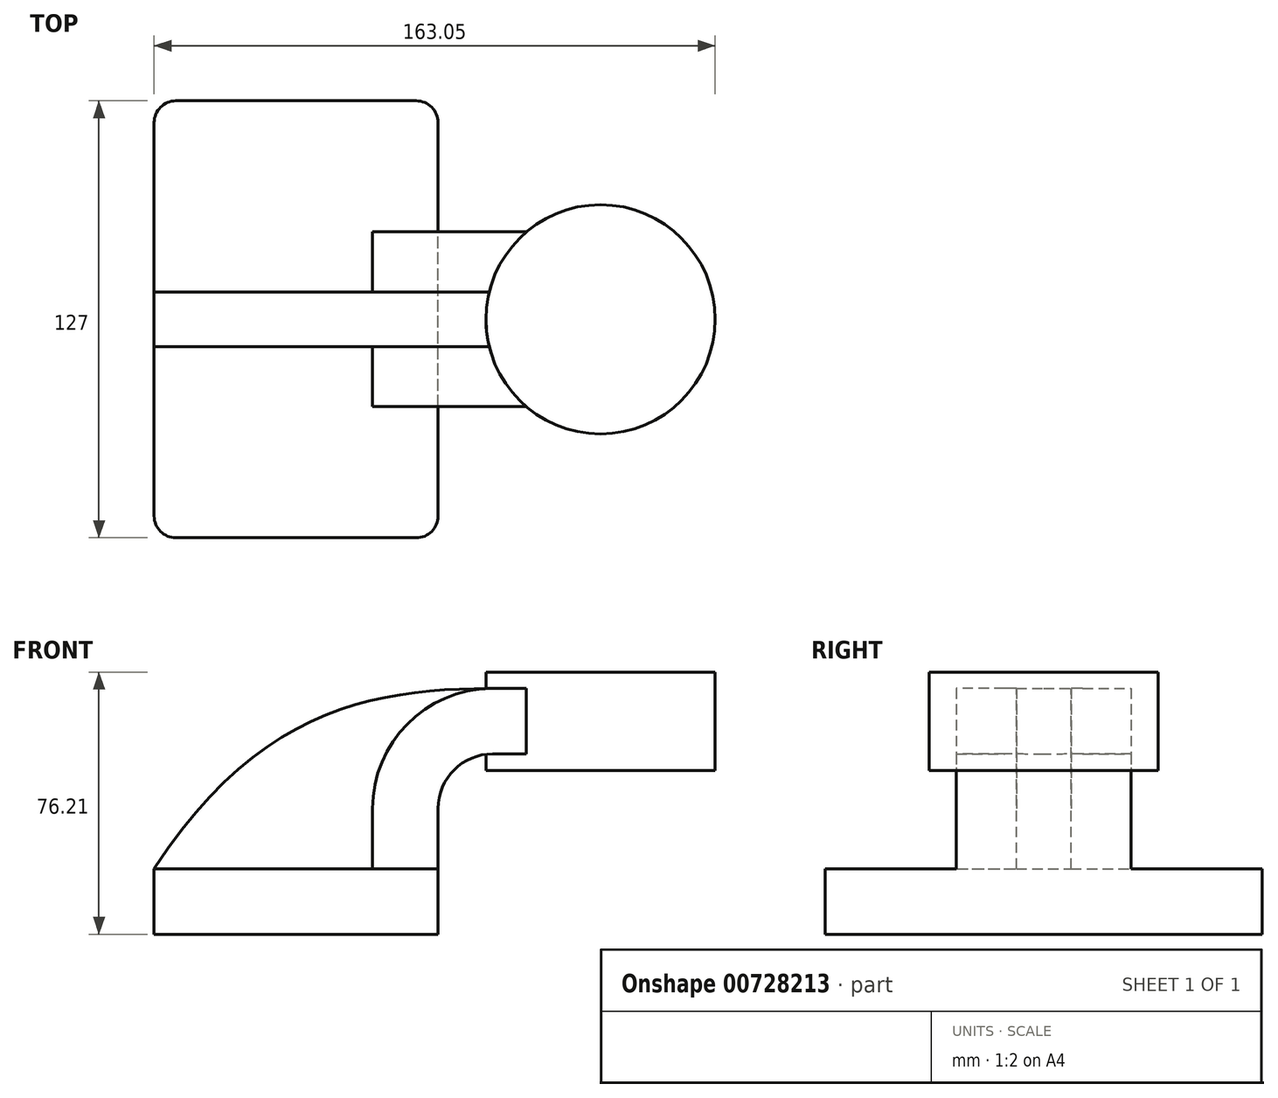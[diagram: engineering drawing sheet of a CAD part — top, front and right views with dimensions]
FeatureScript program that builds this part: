
annotation { "Feature Type Name" : "Feature", "Feature Type Description" : "" }
export const myFeature = defineFeature(function(context is Context, id is Id, definition is map)
    precondition{}
    {
        {
            var Q0;
            Q0=qCreatedBy(makeId("Front.planeOp"),FACE);
            var sketch = newSketch(context, id + "F0", { "sketchPlane" : qUnion([Q0])});
            skLineSegment(sketch, "E0.bottom", {"start": v(41.27, 9.53) * mm, "end": v(-41.28, 9.53) * mm});
            skLineSegment(sketch, "E0.top", {"start": v(41.28, -9.52) * mm, "end": v(-41.27, -9.52) * mm});
            skLineSegment(sketch, "E0.left", {"start": v(41.28, 9.53) * mm, "end": v(41.28, -9.52) * mm});
            skLineSegment(sketch, "E0.right", {"start": v(-41.28, 9.53) * mm, "end": v(-41.27, -9.52) * mm});
            skPoint(sketch, "E0.middle", {"position": v(0, 0) * mm});
            skLineSegment(sketch, "E1.bottom", {"start": v(70.97, 66.68) * mm, "end": v(121.77, 66.68) * mm});
            skLineSegment(sketch, "E1.top", {"start": v(70.97, 38.1) * mm, "end": v(121.77, 38.1) * mm});
            skLineSegment(sketch, "E1.left", {"start": v(70.97, 66.68) * mm, "end": v(70.97, 38.1) * mm});
            skLineSegment(sketch, "E1.right", {"start": v(121.77, 66.68) * mm, "end": v(121.77, 38.1) * mm});
            skPoint(sketch, "E1.middle", {"position": v(96.37, 52.39) * mm});
            skLineSegment(sketch, "E2", {"start": v(41.27, 9.53) * mm, "end": v(41.27, 27) * mm});
            skArc(sketch, "E3", {"start": v(41.27, 27) * mm, "mid": v(45.92, 38.23) * mm, "end": v(57.15, 42.88) * mm});
            skLineSegment(sketch, "E4", {"start": v(57.15, 42.88) * mm, "end": v(88.47, 42.88) * mm});
            skLineSegment(sketch, "E5.0", {"start": v(57.15, 61.93) * mm, "end": v(88.47, 61.93) * mm});
            skArc(sketch, "E5.1", {"start": v(22.23, 27) * mm, "mid": v(32.45, 51.7) * mm, "end": v(57.15, 61.93) * mm});
            skLineSegment(sketch, "E5.2", {"start": v(22.22, 9.53) * mm, "end": v(22.22, 27) * mm});
            skLineSegment(sketch, "E6", {"start": v(88.47, 42.88) * mm, "end": v(88.47, 61.93) * mm});
            skLineSegment(sketch, "E7", {"start": v(88.47, 61.93) * mm, "end": v(88.47, 66.68) * mm});
            skLineSegment(sketch, "E8", {"start": v(88.47, 42.88) * mm, "end": v(88.47, 38.1) * mm});
            skFitSpline(sketch, "E9", {"points": [v(-41.28, 9.52) * mm, v(57.15, 61.93) * mm], "startDerivative": vector(92.37, 142.7) * mm, "endDerivative": vector(100.21, 0.57) * mm});
            skSolve(sketch);
        }
        {
            var Q0;
            Q0=makeQuery(id+"F0.imprint","IMPRINT",FACE,{"disambiguationData":[TD([[makeQuery(id+"F0.imprint","IMPRINT",EDGE,{"derivedFrom":sQuery(id+"F0.wireOp",EDGE,"E0.top")}),-1.0]])]});
            extrude(context, id + "F1", {"entities" : qUnion([Q0]), "endBound" : BoundingType.SYMMETRIC, "depth" : 127 * mm, "offsetDistance" : 25.4 * mm});
        }
        {
            var Q0;
            {var subQ1=sQuery(id+"F0.wireOp",EDGE,"E2");Q0=makeQuery(id+"F0.imprint","IMPRINT",FACE,{"disambiguationData":[TD([[makeQuery(id+"F0.imprint","IMPRINT",EDGE,{"derivedFrom":subQ1}),1.0]])]});}
            var Q1;
            {var subQ5=sQuery(id+"F0.wireOp",EDGE,"E6");Q1=makeQuery(id+"F0.imprint","IMPRINT",FACE,{"disambiguationData":[TD([[makeQuery(id+"F0.imprint","IMPRINT",EDGE,{"derivedFrom":subQ5}),1.0]])]});}
            extrude(context, id + "F2", {"entities" : qUnion([Q0, Q1]), "operationType" : NewBodyOperationType.ADD, "endBound" : BoundingType.SYMMETRIC, "depth" : 50.8 * mm, "offsetDistance" : 25.4 * mm});
        }
        {
            var Q0;
            {var subQ3=sQuery(id+"F0.wireOp",EDGE,"E5.2");Q0=makeQuery(id+"F0.imprint","IMPRINT",FACE,{"disambiguationData":[TD([[makeQuery(id+"F0.imprint","IMPRINT",EDGE,{"derivedFrom":subQ3}),1.0]])]});}
            extrude(context, id + "F3", {"entities" : qUnion([Q0]), "operationType" : NewBodyOperationType.ADD, "endBound" : BoundingType.SYMMETRIC, "depth" : 15.88 * mm, "offsetDistance" : 25.4 * mm});
        }
        {
            var Q0;
            {var subQ0=sQuery(id+"F0.wireOp",EDGE,"E1.right");Q0=makeQuery(id+"F0.imprint","IMPRINT",FACE,{"disambiguationData":[TD([[makeQuery(id+"F0.imprint","IMPRINT",EDGE,{"derivedFrom":subQ0}),-1.0]])]});}
            var Q1;
            Q1=sQuery(id+"F0.wireOp",EDGE,"E6");
            revolve(context, id + "F4", {"operationType" : NewBodyOperationType.ADD, "surfaceOperationType" : NewSurfaceOperationType.NEW, "entities" : qUnion([Q0]), "axis" : qUnion([Q1]), "revolveType" : RevolveType.FULL});
        }
        {
            var Q0;
            Q0=makeQuery(id+"F1.opExtrude","CAP_EDGE",EDGE,{"disambiguationData":[OSD([sQuery(id+"F0.wireOp",EDGE,"E0.left")])],"isStart":false});
            var Q1;
            Q1=makeQuery(id+"F1.opExtrude","CAP_EDGE",EDGE,{"disambiguationData":[OSD([sQuery(id+"F0.wireOp",EDGE,"E0.right")])],"isStart":false});
            var Q2;
            Q2=makeQuery(id+"F1.opExtrude","CAP_EDGE",EDGE,{"disambiguationData":[OSD([sQuery(id+"F0.wireOp",EDGE,"E0.right")])],"isStart":true});
            var Q3;
            Q3=makeQuery(id+"F1.opExtrude","CAP_EDGE",EDGE,{"disambiguationData":[OSD([sQuery(id+"F0.wireOp",EDGE,"E0.left")])],"isStart":true});
            fillet(context, id + "F5", {"entities" : qUnion([Q0, Q1, Q2, Q3]), "radius" : 6.35 * mm, "tangentPropagation" : true, "allowEdgeOverflow" : false});
        }
    });
